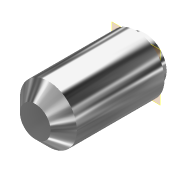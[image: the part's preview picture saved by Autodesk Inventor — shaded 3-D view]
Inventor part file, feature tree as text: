
AUTODESK INVENTOR PART (.ipt)
format: ipt  version: 2019 (Build 230136000, 136)  size: 106,496 bytes
history: native  units: mm
features: extrude x2, sketch x2, plane x1, chamfer x1
ambient origin geometry x8: Origin, YZ Plane, XZ Plane, XY Plane, X Axis, Y Axis, Z Axis, Center Point
bodies: Solid1 (feature_tree)
feature tree (6):
  plane  "Work Plane3"
  extrude  "Extrusion1"  Depth=46.0mm TaperAngle=0.0deg
  chamfer  "Chamfer2"  Distance=6.0mm Angle=45.0deg
  extrude  "Extrusion2"  Depth=4.0mm TaperAngle=0.0deg
  sketch  "Sketch2"  dims[d0=26.0mm d1=46.0mm d2=0.0mm d6=6.0mm d7=2.0mm d8=45.0deg]
  sketch  "Sketch3"  dims[d9=20.0mm d10=4.0mm d11=0.0mm]
